# Revit family: Sanitary_Shower-screens_Duscholux_Giro_Pivot-door-shower
name_source: partatom
category: Plumbing Fixtures
revit_build: Autodesk Revit 2016 (Build: 20150220_1215(x64)
units: mm (PartAtom-declared; Revit-internal decimal feet)

## family parameters
Always vertical = Yes
Cut with Voids When Loaded = No
OmniClass Number = 23.45.00.00
OmniClass Title = Sanitary, Laundry, and Cleaning Equipment
Part Type = Normal
Room Calculation Point = No
Round Connector Dimension = Use Diameter
Shared = No
Work Plane-Based = No

## types (3) — shared parameters
Assembly Code = C1030200
Brand = Duscholux
Certified Quality UNE EN 14428 = http://www.duscholux.es
Combinations = Lateral 90° / Lateral180°
Components = Eropean components
Configuration enclosure = http://configuratumampara.duscholux.es
Description = Front 1 pivot door at 180° for shower
Design country = Spain / Germany
Edition number = 1
Environmental Management ISO 14001 = ECOEMBES Certificate
Fact Sheet = http://blob.duscholux.es
Glass Material = Glass_Material-Duscholux
Glass in Building UNE EN 12150 = CE Conformity marking
IFC Classification = Furnishing Element
Image = http://www.duscholux.es
Maintenance and Cleaning = http://www.duscholux.es
Manufacturer = Duscholux Ibérica, S.A.
Manufacturer country = Spain
Manufacturer name = Duscholux Ibérica, S.A.
NBS Reference Code = 45-35-70
NBS Reference Description = Shower Enclosures
Net Weight (Kg) = 20
Opening System = Pivot Door
Opening System Image = http://blob.duscholux.es
Opening angle = 0.00°
Product family = Plus Evolution Giro
Product group = Front for shower
Products = http://www.duscholux.es
Ref. = 7UI / 7UD
Series = Plus Evolution Giro
Technical Inspection Certificate (Applus) = http://www.duscholux.es
Thickness Glass = 5 mm  [stored 0.0164042 ft]
UNSPSC Code = 30181507
URL = http://www.duscholux.es
Uniclass 2015 Code = PR-40-20-06-79
Uniclass 2015 Description = Shower Enclosures

## per-type parameters (varying)
| type | Accesories Material | Door aperture | Frame Material | Handle Height | Handle Material | Height | Max Height | Min Max Width | Width |
| Shiny silver Finish | Plastic, Gray | 822 mm | Shiny Silver  Aluminium Finish | 900 mm  [stored 2.95276 ft] | Matt Silver Aluminium Finish | 1800 mm  [stored 5.90551 ft] | 1800 mm  [stored 5.90551 ft] | 900 mm  [stored 2.95276 ft] | 900 mm  [stored 2.95276 ft] |
| White Aluminium Finish | White Finish | 772 mm | White Aluminium Finish | 900 mm  [stored 2.95276 ft] | White Finish | 1800 mm  [stored 5.90551 ft] | 1800 mm  [stored 5.90551 ft] | 850 mm  [stored 2.78871 ft] | 850 mm  [stored 2.78871 ft] |
| Silver Matt Aluminium Finish | Plastic, Gray | 1022 mm | Matt Silver Aluminium Finish | 1000 mm  [stored 3.28084 ft] | Matt Silver Aluminium Finish | 2000 mm  [stored 6.56168 ft] | 2000 mm  [stored 6.56168 ft] | 1100 mm | 1400 mm  [stored 4.59318 ft] |

note: [stored X ft] marks values corroborated as IEEE doubles in the binary element streams (Revit-internal decimal feet)
